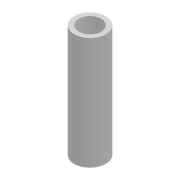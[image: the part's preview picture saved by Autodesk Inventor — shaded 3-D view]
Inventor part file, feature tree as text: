
AUTODESK INVENTOR PART (.ipt)
format: ipt  version: 2018 (Build 220112000, 112)  size: 81,408 bytes
history: native  units: mm
features: extrude x1
ambient origin geometry x8: Origin, YZ Plane, XZ Plane, XY Plane, X Axis, Y Axis, Z Axis, Center Point
bodies: Solid1 (feature_tree)
feature tree (1):
  extrude  "Extrude1"  [1 undecoded]
note: 1 required parameter value undecoded (feature->parameter linkage not recoverable at this tier; creation-order binding heuristic only, values carry confidence <= 0.55)
